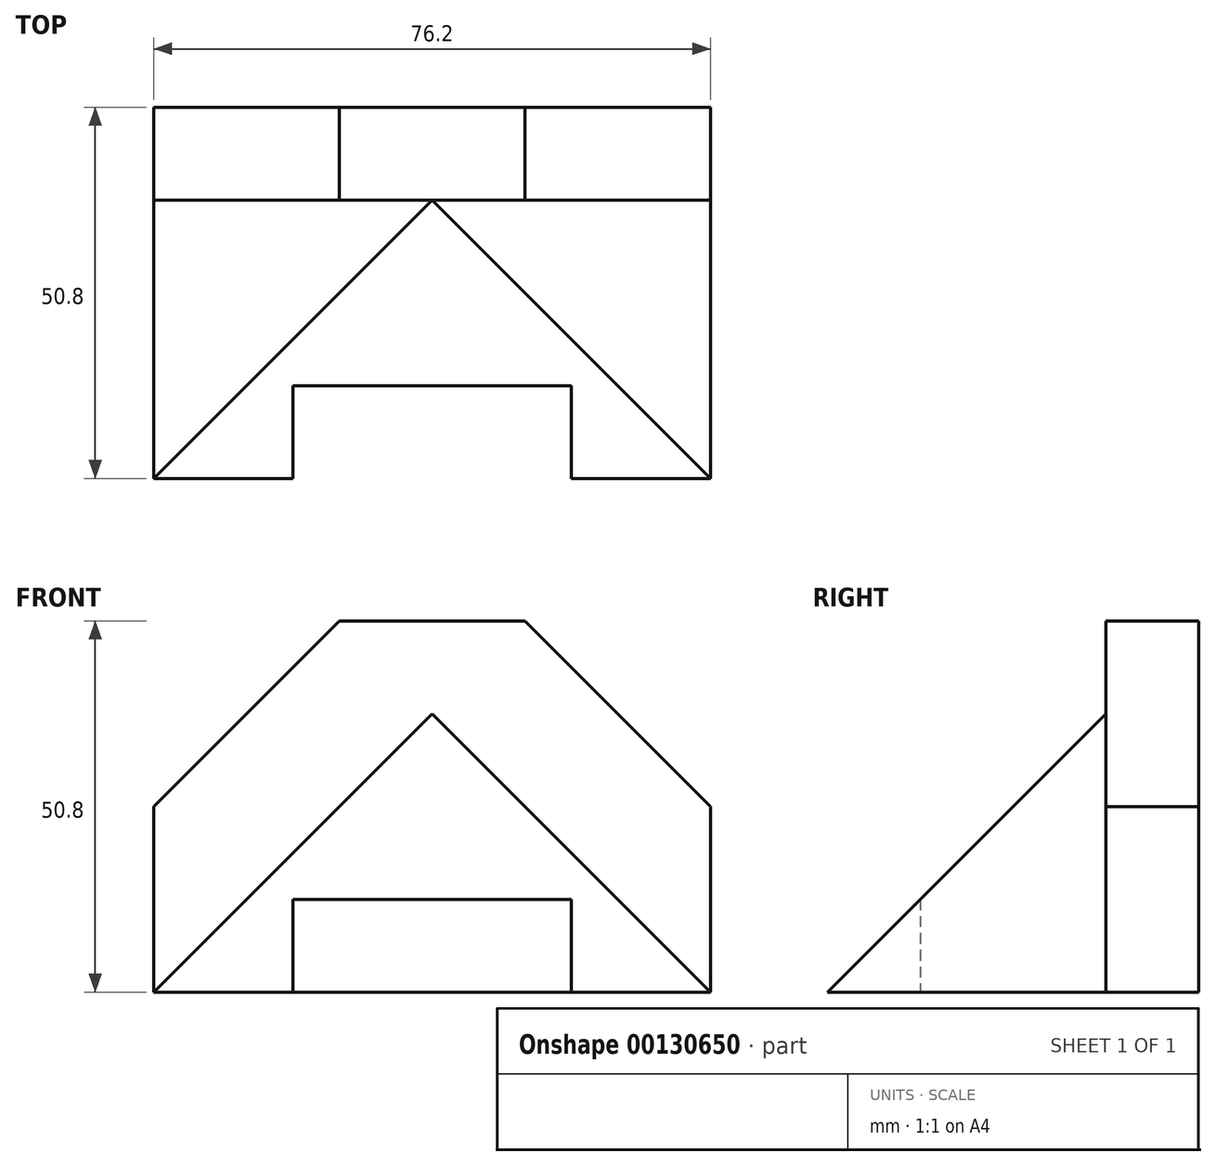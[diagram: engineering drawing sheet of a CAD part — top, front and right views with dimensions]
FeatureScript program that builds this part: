
annotation { "Feature Type Name" : "Feature", "Feature Type Description" : "" }
export const myFeature = defineFeature(function(context is Context, id is Id, definition is map)
    precondition{}
    {
        {
            var Q0;
            Q0=qCreatedBy(makeId("Front.planeOp"),FACE);
            var sketch = newSketch(context, id + "F0", { "sketchPlane" : qUnion([Q0])});
            skLineSegment(sketch, "E0", {"start": v(-19.05, 0) * mm, "end": v(-19.05, 12.7) * mm});
            skLineSegment(sketch, "E1", {"start": v(-19.05, 12.7) * mm, "end": v(19.05, 12.7) * mm});
            skLineSegment(sketch, "E2", {"start": v(19.05, 12.7) * mm, "end": v(19.05, 0) * mm});
            skLineSegment(sketch, "E3", {"start": v(19.05, 0) * mm, "end": v(-19.05, 0) * mm});
            skLineSegment(sketch, "E4", {"start": v(-19.05, 0) * mm, "end": v(-38.1, 0) * mm});
            skLineSegment(sketch, "E5", {"start": v(-38.1, 0) * mm, "end": v(-38.1, 25.4) * mm});
            skLineSegment(sketch, "E6", {"start": v(-12.7, 50.8) * mm, "end": v(12.7, 50.8) * mm});
            skLineSegment(sketch, "E7", {"start": v(12.7, 50.8) * mm, "end": v(38.1, 25.4) * mm});
            skLineSegment(sketch, "E8", {"start": v(38.1, 25.4) * mm, "end": v(38.1, 0) * mm});
            skLineSegment(sketch, "E9", {"start": v(38.1, 0) * mm, "end": v(0, 38.1) * mm});
            skLineSegment(sketch, "E10", {"start": v(0, 38.1) * mm, "end": v(-38.1, 0) * mm});
            skLineSegment(sketch, "E11", {"start": v(-38.1, 0) * mm, "end": v(-19.05, 0) * mm});
            skLineSegment(sketch, "E12", {"start": v(19.05, 0) * mm, "end": v(38.1, 0) * mm});
            skLineSegment(sketch, "E13", {"start": v(-38.1, 25.4) * mm, "end": v(-12.7, 50.8) * mm});
            skSolve(sketch);
        }
        {
            var Q0;
            Q0 = qSketchRegion(id + "F0", true);
            extrude(context, id + "F1", {"entities" : qUnion([Q0]), "endBound" : BoundingType.SYMMETRIC, "depth" : 50.8 * mm});
        }
        {
            var Q0;
            Q0=qCreatedBy(makeId("Top.planeOp"),FACE);
            var sketch = newSketch(context, id + "F2", { "sketchPlane" : qUnion([Q0])});
            skLineSegment(sketch, "E14", {"start": v(-19.05, -25.4) * mm, "end": v(-19.05, -12.7) * mm});
            skLineSegment(sketch, "E15", {"start": v(-19.05, -12.7) * mm, "end": v(19.05, -12.7) * mm});
            skLineSegment(sketch, "E16", {"start": v(19.05, -12.7) * mm, "end": v(19.05, -25.4) * mm});
            skLineSegment(sketch, "E17", {"start": v(19.05, -25.4) * mm, "end": v(-19.05, -25.4) * mm});
            skSolve(sketch);
        }
        {
            var Q0;
            Q0 = qSketchRegion(id + "F2", true);
            extrude(context, id + "F3", {"entities" : qUnion([Q0]), "operationType" : NewBodyOperationType.REMOVE, "endBound" : BoundingType.THROUGH_ALL, "depth" : 25.4 * mm});
        }
        {
            var Q0;
            Q0=qCreatedBy(makeId("Right.planeOp"),FACE);
            var sketch = newSketch(context, id + "F4", { "sketchPlane" : qUnion([Q0])});
            skLineSegment(sketch, "E18", {"start": v(-25.4, 0) * mm, "end": v(12.7, 38.1) * mm});
            skLineSegment(sketch, "E19", {"start": v(12.7, 38.1) * mm, "end": v(12.7, 0) * mm});
            skLineSegment(sketch, "E20", {"start": v(12.7, 0) * mm, "end": v(-25.4, 0) * mm});
            skLineSegment(sketch, "E21", {"start": v(-25.4, 0) * mm, "end": v(-25.4, 50.8) * mm});
            skLineSegment(sketch, "E22", {"start": v(-25.4, 50.8) * mm, "end": v(12.7, 50.8) * mm});
            skLineSegment(sketch, "E23", {"start": v(12.7, 50.8) * mm, "end": v(12.7, 38.1) * mm});
            skSolve(sketch);
        }
        {
            var Q0;
            Q0=makeQuery(id+"F4.imprint","IMPRINT",FACE,{"disambiguationData":[TD([[makeQuery(id+"F4.imprint","IMPRINT",EDGE,{"derivedFrom":sQuery(id+"F4.wireOp",EDGE,"E18")}),1.0]])]});
            extrude(context, id + "F5", {"entities" : qUnion([Q0]), "operationType" : NewBodyOperationType.REMOVE, "endBound" : BoundingType.SYMMETRIC, "depth" : 76.2 * mm});
        }
        {
            var Q0;
            Q0=qCreatedBy(makeId("Front.planeOp"),FACE);
            var sketch = newSketch(context, id + "F6", { "sketchPlane" : qUnion([Q0])});
            skLineSegment(sketch, "E24.0", {"start": v(38.1, 0) * mm, "end": v(0, 38.1) * mm});
            skLineSegment(sketch, "E25.0", {"start": v(0, 38.1) * mm, "end": v(-38.1, 0) * mm});
            skLineSegment(sketch, "E26.0", {"start": v(-38.1, 0) * mm, "end": v(-38.1, 25.4) * mm});
            skLineSegment(sketch, "E27.0", {"start": v(-38.1, 25.4) * mm, "end": v(-25.4, 38.1) * mm});
            skLineSegment(sketch, "E28.0", {"start": v(25.4, 38.1) * mm, "end": v(-25.4, 38.1) * mm});
            skLineSegment(sketch, "E29.0", {"start": v(25.4, 38.1) * mm, "end": v(38.1, 25.4) * mm});
            skLineSegment(sketch, "E30.0", {"start": v(38.1, 25.4) * mm, "end": v(38.1, 0) * mm});
            skSolve(sketch);
        }
        {
            var Q0;
            {var subQ0=sQuery(id+"F6.wireOp",EDGE,"E25.0");Q0=makeQuery(id+"F6.imprint","IMPRINT",FACE,{"disambiguationData":[TD([[makeQuery(id+"F6.imprint","IMPRINT",EDGE,{"derivedFrom":subQ0}),-1.0]])]});}
            extrude(context, id + "F7", {"entities" : qUnion([Q0]), "operationType" : NewBodyOperationType.REMOVE, "oppositeDirection" : true, "depth" : 12.7 * mm, "hasSecondDirection" : true, "secondDirectionOppositeDirection" : false, "secondDirectionDepth" : 25.4 * mm});
        }
        {
            var Q0;
            {var subQ0=sQuery(id+"F6.wireOp",EDGE,"E24.0");Q0=makeQuery(id+"F6.imprint","IMPRINT",FACE,{"disambiguationData":[TD([[makeQuery(id+"F6.imprint","IMPRINT",EDGE,{"derivedFrom":subQ0}),-1.0]])]});}
            extrude(context, id + "F8", {"entities" : qUnion([Q0]), "operationType" : NewBodyOperationType.REMOVE, "depth" : 25.4 * mm, "hasSecondDirection" : true, "secondDirectionOppositeDirection" : true, "secondDirectionDepth" : 12.7 * mm});
        }
    });
